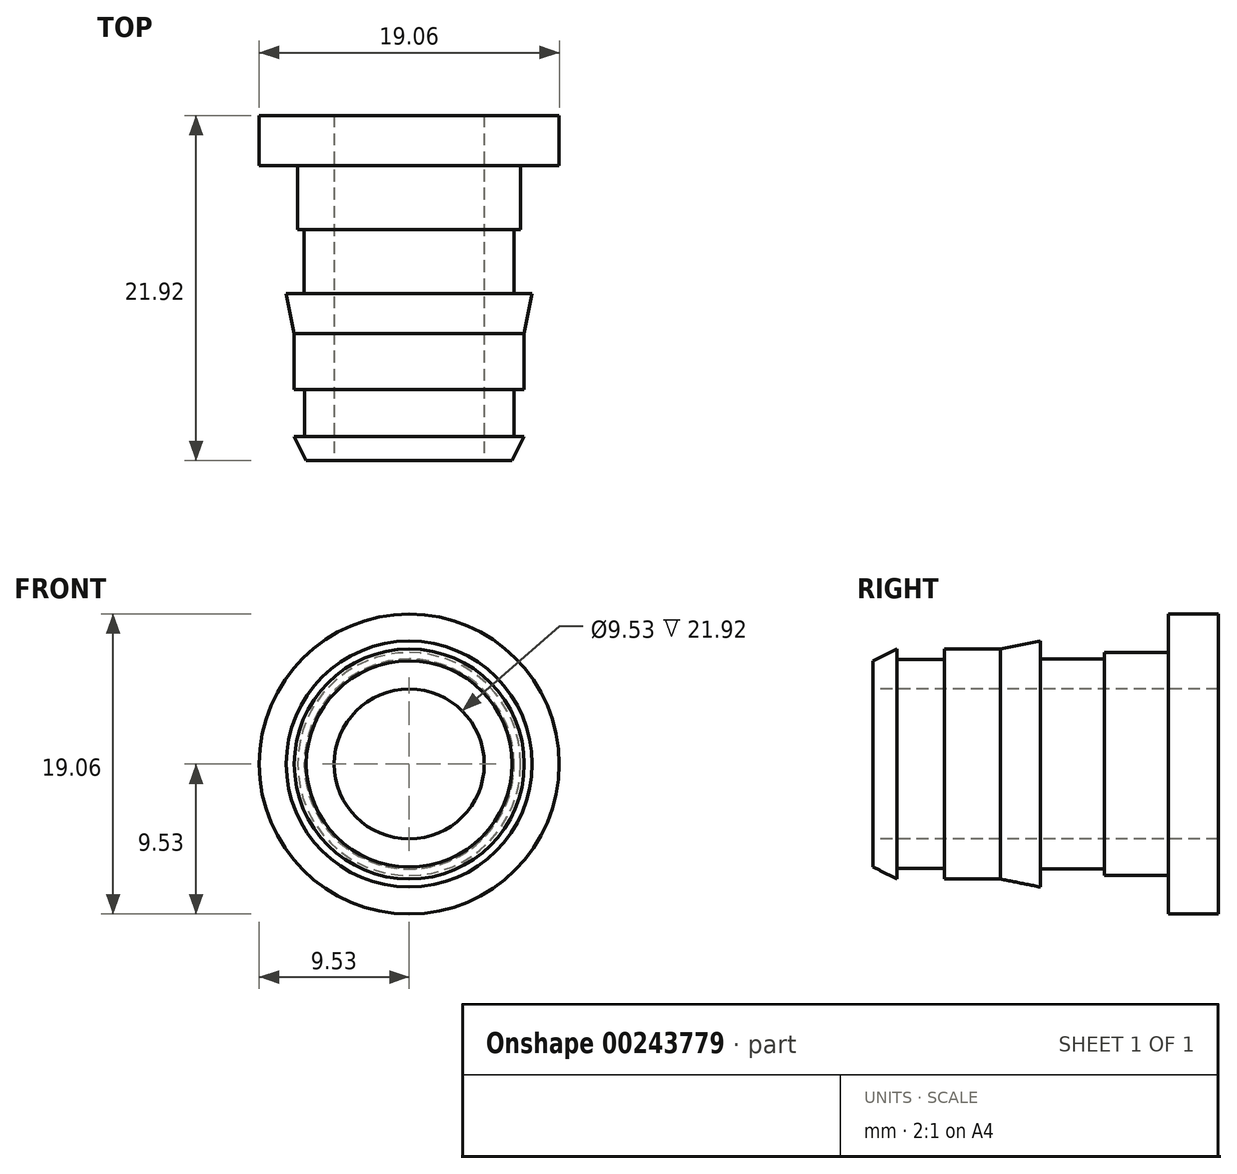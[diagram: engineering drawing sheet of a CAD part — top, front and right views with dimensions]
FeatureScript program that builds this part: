
annotation { "Feature Type Name" : "Feature", "Feature Type Description" : "" }
export const myFeature = defineFeature(function(context is Context, id is Id, definition is map)
    precondition{}
    {
        {
            var Q0;
            Q0=qCreatedBy(makeId("Front.planeOp"),FACE);
            var sketch = newSketch(context, id + "F0", { "sketchPlane" : qUnion([Q0])});
            skCircle(sketch, "E0", {"center": v(0, 0) * mm, "radius": 9.53 * mm});
            skSolve(sketch);
        }
        {
            var Q0;
            Q0 = qSketchRegion(id + "F0", true);
            extrude(context, id + "F1", {"entities" : qUnion([Q0]), "depth" : 3.17 * mm});
        }
        {
            var Q0;
            Q0=makeQuery(id+"F1.opExtrude","CAP_FACE",FACE,{"disambiguationData":[OSD([sQuery(id+"F0.wireOp",EDGE,"E0")])],"isStart":false});
            var sketch = newSketch(context, id + "F2", { "sketchPlane" : qUnion([Q0])});
            skCircle(sketch, "E1", {"center": v(0, 0) * mm, "radius": 7.08 * mm});
            skSolve(sketch);
        }
        {
            var Q0;
            Q0 = qSketchRegion(id + "F2", true);
            extrude(context, id + "F3", {"entities" : qUnion([Q0]), "operationType" : NewBodyOperationType.ADD, "depth" : 4.06 * mm});
        }
        {
            var Q0;
            Q0=makeQuery(id+"F3.opExtrude","CAP_FACE",FACE,{"disambiguationData":[OSD([sQuery(id+"F2.wireOp",EDGE,"E1")])],"isStart":false});
            var sketch = newSketch(context, id + "F4", { "sketchPlane" : qUnion([Q0])});
            skCircle(sketch, "E2", {"center": v(0, 0) * mm, "radius": 6.67 * mm});
            skSolve(sketch);
        }
        {
            var Q0;
            Q0 = qSketchRegion(id + "F4", true);
            extrude(context, id + "F5", {"entities" : qUnion([Q0]), "operationType" : NewBodyOperationType.ADD, "depth" : 4.06 * mm});
        }
        {
            var Q0;
            Q0=makeQuery(id+"F5.opExtrude","CAP_FACE",FACE,{"disambiguationData":[OSD([sQuery(id+"F4.wireOp",EDGE,"E2")])],"isStart":false});
            var sketch = newSketch(context, id + "F6", { "sketchPlane" : qUnion([Q0])});
            skCircle(sketch, "E3", {"center": v(0, 0) * mm, "radius": 7.81 * mm});
            skSolve(sketch);
        }
        {
            var Q0;
            Q0 = qSketchRegion(id + "F6", true);
            extrude(context, id + "F7", {"entities" : qUnion([Q0]), "operationType" : NewBodyOperationType.ADD, "depth" : 2.54 * mm});
        }
        {
            var Q0;
            Q0=makeQuery(id+"F7.opExtrude","CAP_FACE",FACE,{"disambiguationData":[OSD([sQuery(id+"F6.wireOp",EDGE,"E3")])],"isStart":false});
            var sketch = newSketch(context, id + "F8", { "sketchPlane" : qUnion([Q0])});
            skCircle(sketch, "E4", {"center": v(0, 0) * mm, "radius": 7.3 * mm});
            skSolve(sketch);
        }
        {
            var Q0;
            Q0 = qSketchRegion(id + "F8", true);
            extrude(context, id + "F9", {"entities" : qUnion([Q0]), "operationType" : NewBodyOperationType.ADD, "depth" : 3.56 * mm});
        }
        {
            var Q0;
            Q0=makeQuery(id+"F9.opExtrude","CAP_FACE",FACE,{"disambiguationData":[OSD([sQuery(id+"F8.wireOp",EDGE,"E4")])],"isStart":false});
            var sketch = newSketch(context, id + "F10", { "sketchPlane" : qUnion([Q0])});
            skCircle(sketch, "E5", {"center": v(0, 0) * mm, "radius": 6.64 * mm});
            skSolve(sketch);
        }
        {
            var Q0;
            Q0 = qSketchRegion(id + "F10", true);
            extrude(context, id + "F11", {"entities" : qUnion([Q0]), "operationType" : NewBodyOperationType.ADD, "depth" : 3 * mm});
        }
        {
            var Q0;
            Q0=makeQuery(id+"F11.opExtrude","CAP_FACE",FACE,{"disambiguationData":[OSD([sQuery(id+"F10.wireOp",EDGE,"E5")])],"isStart":false});
            var sketch = newSketch(context, id + "F12", { "sketchPlane" : qUnion([Q0])});
            skCircle(sketch, "E6", {"center": v(0, 0) * mm, "radius": 7.3 * mm});
            skSolve(sketch);
        }
        {
            var Q0;
            Q0 = qSketchRegion(id + "F12", true);
            extrude(context, id + "F13", {"entities" : qUnion([Q0]), "operationType" : NewBodyOperationType.ADD, "depth" : 1.52 * mm});
        }
        {
            var Q0;
            Q0=makeQuery(id+"F7.opExtrude","CAP_EDGE",EDGE,{"disambiguationData":[OSD([sQuery(id+"F6.wireOp",EDGE,"E3")])],"isStart":false});
            chamfer(context, id + "F14", {"entities" : qUnion([Q0]), "chamferType" : ChamferType.TWO_OFFSETS, "width1" : 0.5 * mm, "oppositeDirection" : false, "width2" : 2.54 * mm, "tangentPropagation" : true});
        }
        {
            var Q0;
            Q0=makeQuery(id+"F13.opExtrude","CAP_EDGE",EDGE,{"disambiguationData":[OSD([sQuery(id+"F12.wireOp",EDGE,"E6")])],"isStart":false});
            chamfer(context, id + "F15", {"entities" : qUnion([Q0]), "chamferType" : ChamferType.TWO_OFFSETS, "width1" : 0.76 * mm, "oppositeDirection" : false, "width2" : 1.52 * mm, "tangentPropagation" : true});
        }
        {
            var Q0;
            Q0=makeQuery(id+"F13.opExtrude","CAP_FACE",FACE,{"disambiguationData":[OSD([sQuery(id+"F12.wireOp",EDGE,"E6")])],"isStart":false});
            var sketch = newSketch(context, id + "F16", { "sketchPlane" : qUnion([Q0])});
            skCircle(sketch, "E7", {"center": v(0, 0) * mm, "radius": 4.76 * mm});
            skSolve(sketch);
        }
        {
            var Q0;
            Q0 = qSketchRegion(id + "F16", true);
            extrude(context, id + "F17", {"entities" : qUnion([Q0]), "operationType" : NewBodyOperationType.REMOVE, "endBound" : BoundingType.THROUGH_ALL, "oppositeDirection" : true, "depth" : 25.4 * mm});
        }
    });
